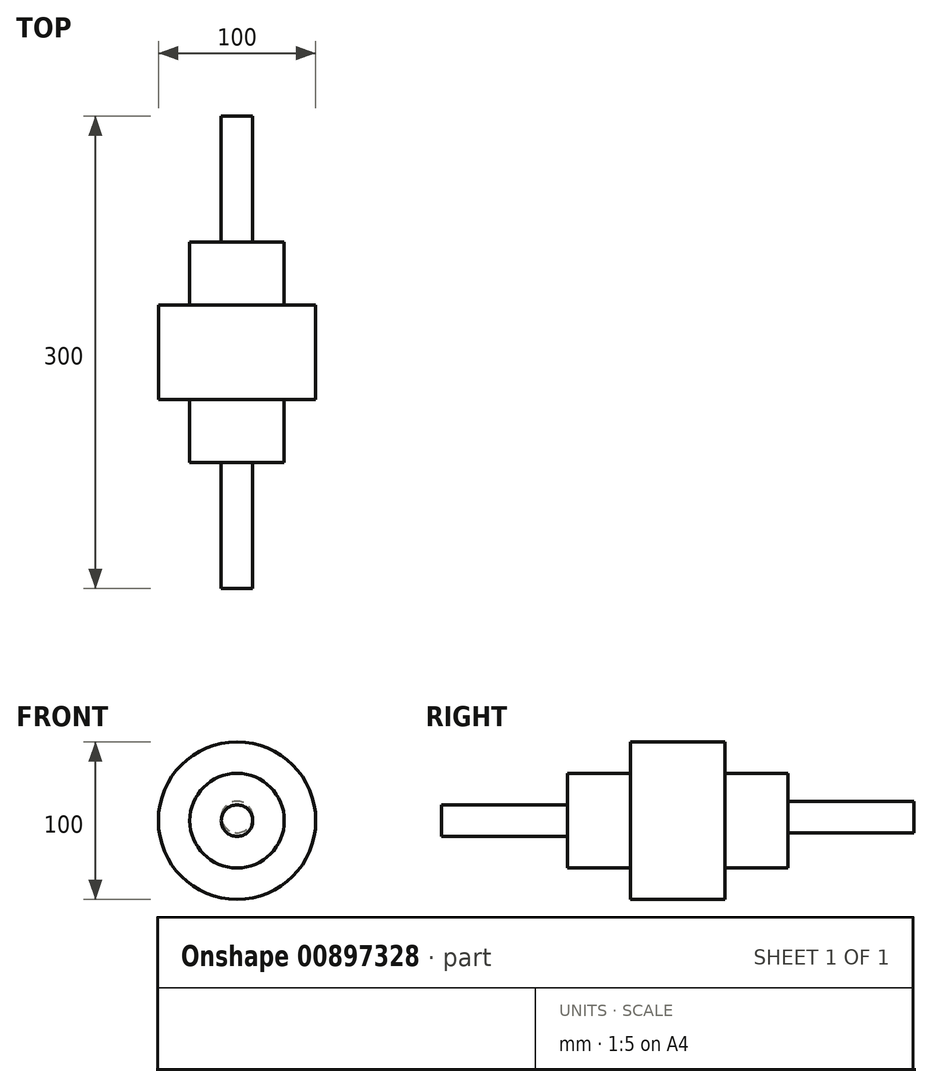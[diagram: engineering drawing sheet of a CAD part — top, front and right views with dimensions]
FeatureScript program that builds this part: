
annotation { "Feature Type Name" : "Feature", "Feature Type Description" : "" }
export const myFeature = defineFeature(function(context is Context, id is Id, definition is map)
    precondition{}
    {
        {
            var Q0;
            Q0=qCreatedBy(makeId("Front.planeOp"),FACE);
            var sketch = newSketch(context, id + "F0", { "sketchPlane" : qUnion([Q0])});
            skCircle(sketch, "E0", {"center": v(0, 0) * mm, "radius": 50 * mm});
            skSolve(sketch);
        }
        {
            var Q0;
            Q0=makeQuery(id+"F0.imprint","IMPRINT",FACE,{"disambiguationData":[TD([[makeQuery(id+"F0.imprint","IMPRINT",EDGE,{"derivedFrom":sQuery(id+"F0.wireOp",EDGE,"E0")}),1.0]])]});
            extrude(context, id + "F1", {"entities" : qUnion([Q0]), "depth" : 60 * mm, "offsetDistance" : 25.4 * mm});
        }
        {
            var Q0;
            Q0=makeQuery(id+"F0.imprint","IMPRINT",FACE,{"disambiguationData":[TD([[makeQuery(id+"F0.imprint","IMPRINT",EDGE,{"derivedFrom":sQuery(id+"F0.wireOp",EDGE,"E0")}),1.0]])]});
            var sketch = newSketch(context, id + "F2", { "sketchPlane" : qUnion([Q0])});
            skCircle(sketch, "E1", {"center": v(0, 0) * mm, "radius": 30 * mm});
            skSolve(sketch);
        }
        {
            var Q0;
            Q0=makeQuery(id+"F2.imprint","IMPRINT",FACE,{"disambiguationData":[TD([[makeQuery(id+"F2.imprint","IMPRINT",EDGE,{"derivedFrom":sQuery(id+"F2.wireOp",EDGE,"E1")}),1.0]])]});
            extrude(context, id + "F3", {"entities" : qUnion([Q0]), "operationType" : NewBodyOperationType.ADD, "oppositeDirection" : true, "depth" : 40 * mm, "offsetDistance" : 25.4 * mm});
        }
        {
            var Q0;
            Q0=makeQuery(id+"F3.opExtrude","CAP_FACE",FACE,{"disambiguationData":[OSD([sQuery(id+"F2.wireOp",EDGE,"E1")])],"isStart":false});
            var sketch = newSketch(context, id + "F4", { "sketchPlane" : qUnion([Q0])});
            skCircle(sketch, "E2", {"center": v(0, 2.32) * mm, "radius": 10 * mm});
            skSolve(sketch);
        }
        {
            var Q0;
            Q0=makeQuery(id+"F4.imprint","IMPRINT",FACE,{"disambiguationData":[TD([[makeQuery(id+"F4.imprint","IMPRINT",EDGE,{"derivedFrom":sQuery(id+"F4.wireOp",EDGE,"E2")}),1.0]])]});
            extrude(context, id + "F5", {"entities" : qUnion([Q0]), "operationType" : NewBodyOperationType.ADD, "depth" : 80 * mm, "offsetDistance" : 25.4 * mm});
        }
        {
            var Q0;
            Q0=makeQuery(id+"F1.opExtrude","CAP_FACE",FACE,{"disambiguationData":[OSD([sQuery(id+"F0.wireOp",EDGE,"E0")])],"isStart":false});
            var sketch = newSketch(context, id + "F6", { "sketchPlane" : qUnion([Q0])});
            skCircle(sketch, "E3", {"center": v(0, 0) * mm, "radius": 30 * mm});
            skSolve(sketch);
        }
        {
            var Q0;
            Q0=makeQuery(id+"F6.imprint","IMPRINT",FACE,{"disambiguationData":[TD([[makeQuery(id+"F6.imprint","IMPRINT",EDGE,{"derivedFrom":sQuery(id+"F6.wireOp",EDGE,"E3")}),1.0]])]});
            extrude(context, id + "F7", {"entities" : qUnion([Q0]), "operationType" : NewBodyOperationType.ADD, "depth" : 40 * mm, "offsetDistance" : 25.4 * mm});
        }
        {
            var Q0;
            Q0=makeQuery(id+"F7.opExtrude","CAP_FACE",FACE,{"disambiguationData":[OSD([sQuery(id+"F6.wireOp",EDGE,"E3")])],"isStart":false});
            var sketch = newSketch(context, id + "F8", { "sketchPlane" : qUnion([Q0])});
            skCircle(sketch, "E4", {"center": v(0, 0) * mm, "radius": 10 * mm});
            skSolve(sketch);
        }
        {
            var Q0;
            Q0=makeQuery(id+"F8.imprint","IMPRINT",FACE,{"disambiguationData":[TD([[makeQuery(id+"F8.imprint","IMPRINT",EDGE,{"derivedFrom":sQuery(id+"F8.wireOp",EDGE,"E4")}),1.0]])]});
            var Q1;
            Q1=sQuery(id+"F8.wireOp",EDGE,"E4");
            extrude(context, id + "F9", {"entities" : qUnion([Q0]), "operationType" : NewBodyOperationType.ADD, "surfaceOperationType" : NewSurfaceOperationType.ADD, "surfaceEntities" : qUnion([Q1]), "depth" : 80 * mm, "offsetDistance" : 25.4 * mm});
        }
    });
